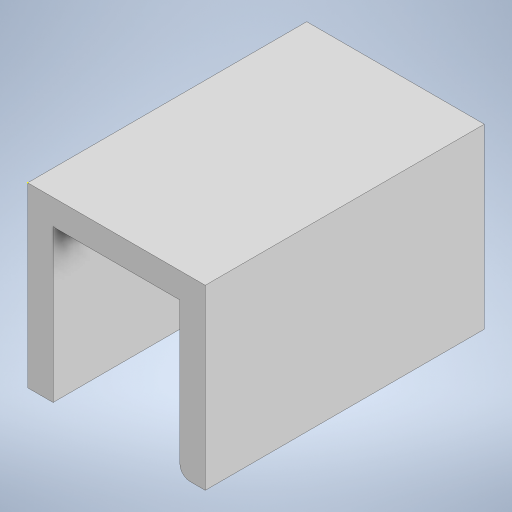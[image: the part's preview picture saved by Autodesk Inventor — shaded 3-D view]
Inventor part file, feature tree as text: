
AUTODESK INVENTOR PART (.ipt)
format: ipt  version: 2023 (Build 270158000, 158)  size: 210,432 bytes
history: native  units: in
note: dims shown in document units (in); Inventor stores cm internally (conversion verified against a paired STEP export)
features: sketch x9, extrude x4, fillet x1
ambient origin geometry x8: Origin, YZ Plane, XZ Plane, XY Plane, X Axis, Y Axis, Z Axis, Center Point
bodies: Solid1 (feature_tree)
feature tree (14):
  extrude  "Extrusion1"  Depth=0.5512in
  extrude  "Extrusion2"  Depth=0.3937in
  sketch  "Sketch8"  dims[d5=0.7874in d6=0.7874in d7=0.0in]
  sketch  "Sketch9"  dims[d30=0.1969in d31=0.4724in d32=0.0787in d33=0.0in]
  sketch  "Sketch11"  dims[d34=0.1772in]
  sketch  "Sketch14"  dims[d35=0.0984in]
  sketch  "Sketch15"  dims[d36=0.3543in d37=0.0in]
  extrude  "Extrusion10"  Depth=0.7874in TaperAngle=0.0deg
  extrude  "Extrusion11"  Depth=0.4724in
  fillet  "Fillet1"  Radius=0.0787in
  sketch  "Sketch1"  dims[d0=0.5512in d1=0.5512in]
  sketch  "Sketch2"  dims[d2=0.8661in d3=0.0in d4=0.3937in]
  sketch  "Sketch16"  dims[d38=0.0315in]
  sketch  "Sketch17"  dims[d39=0.0in d40=0.0in d41=0.0in]
